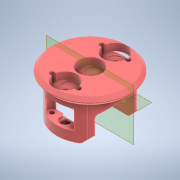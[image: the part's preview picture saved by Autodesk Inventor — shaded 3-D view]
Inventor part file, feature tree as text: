
AUTODESK INVENTOR PART (.ipt)
format: ipt  version: 2022 (Build 260153000, 153)  size: 1,007,616 bytes
history: native  units: in
note: dims shown in document units (in); Inventor stores cm internally (conversion verified against a paired STEP export)
features: extrude x14, sketch x13, fillet x5, projected_geometry x5, mirror x4, other x4, plane x3, reference x2, chamfer x1
ambient origin geometry x8: Origin, YZ Plane, XZ Plane, XY Plane, X Axis, Y Axis, Z Axis, Center Point
bodies: Solid1 (feature_tree)
feature tree (51):
  extrude  "Extrusion1"  Depth=0.2756in TaperAngle=0.0deg
  extrude  "Extrusion2"  Depth=4.0in
  extrude  "Extrusion10"  Depth=1.3681in TaperAngle=0.0deg
  sketch  "Sketch6"  dims[d5=0.25in d6=1.3681in d7=0.0in]
  extrude  "Extrusion6"  Depth=1.0in
  extrude  "Extrusion7"  Depth=0.7874in TaperAngle=360.0deg
  plane  "Work Plane6"
  plane  "Work Plane7"
  extrude  "Extrusion8"  Depth=0.05in TaperAngle=0.0deg
  extrude  "Extrusion9"  [1 undecoded]
  extrude  "Extrusion11"  Depth=1.125in
  fillet  "Fillet3"  Radius=0.3238in
  fillet  "Fillet4"  Radius=0.1in
  fillet  "Fillet5"  Radius=3.0in
  plane  "Work Plane8"
  mirror  "Mirror2"
  extrude  "Extrusion12"  TaperAngle=45.0deg  [1 undecoded]
  mirror  "Mirror3"
  extrude  "Extrusion13"  TaperAngle=0.0deg  [1 undecoded]
  fillet  "Fillet6"  Radius=0.5in
  extrude  "Extrusion14"  Depth=0.125in
  chamfer  "Chamfer2"  Distance=0.5in
  extrude  "Extrusion15"  Depth=0.125in
  mirror  "Mirror4"
  extrude  "Extrusion16"  Depth=0.125in TaperAngle=0.0deg
  extrude  "Extrusion17"  Depth=0.125in
  fillet  "Fillet8"  Radius=0.0472in
  mirror  "Mirror5"
  sketch  "Sketch1"  dims[d0=2.9941in d1=0.2756in d2=0.0in]
  sketch  "Sketch2"  dims[d3=1.5in d4=4.0in]
  projected_geometry  "Projected Loop1"
  sketch  "Sketch7"  dims[d40=0.1839in d41=1.0in]
  sketch  "Sketch8"  dims[d42=0.1679in d43=0.7874in d45=360.0deg]
  reference  "Reference1"
  sketch  "Sketch9"  dims[d47=1.5in d48=0.0in d49=0.05in d50=0.0in]
  projected_geometry  "Projected Loop8"
  sketch  "Sketch10"  dims[d51=0.1749in d52=-0.3556in]
  sketch  "Sketch11"  dims[d55=0.7356in d56=0.0in d57=1.125in d58=0.3238in d59=0.1in d60=0.0in d61=3.0in]
  reference  "Reference2"
  sketch  "Sketch12"  dims[d62=1.0in d63=0.0in d64=45.0deg]
  sketch  "Sketch13"  dims[d65=45.0deg d66=0.0in d67=0.0in d68=0.5in]
  sketch  "Sketch14"  dims[d69=0.125in d70=0.0236in]
  projected_geometry  "Projected Loop9"
  sketch  "Sketch15"  dims[d71=0.1852in]
  projected_geometry  "Projected Loop10"
  sketch  "Sketch16"  dims[d72=0.2in d73=0.5in d74=0.0in d75=0.876in d76=0.2756in d77=0.0in d78=0.0236in d80=0.0472in d81=0.0in d82=0.2559in d84=0.1181in d85=0.125in d86=45.0deg d87=0.1014in d88=0.0in d89=0.3957in d90=0.261in d91=0.0787in d92=0.0in d93=0.261in d94=0.3937in d95=0.0in d96=0.125in d22=0.5in d23=0.0344in d24=0.5in d25=0.0344in d79=0.0344in]
  projected_geometry  "Projected Loop11"
  other  "<userpath>\Documents\CAD\guardSwerve1\Assembly1.iam"
  other  "Assembly1.iam"
  other  "SScrew Star Smooth .750:2"
  other  "2.75 Traction, No Insert:1"
note: 3 required parameter values undecoded (feature->parameter linkage not recoverable at this tier; creation-order binding heuristic only, values carry confidence <= 0.55)
